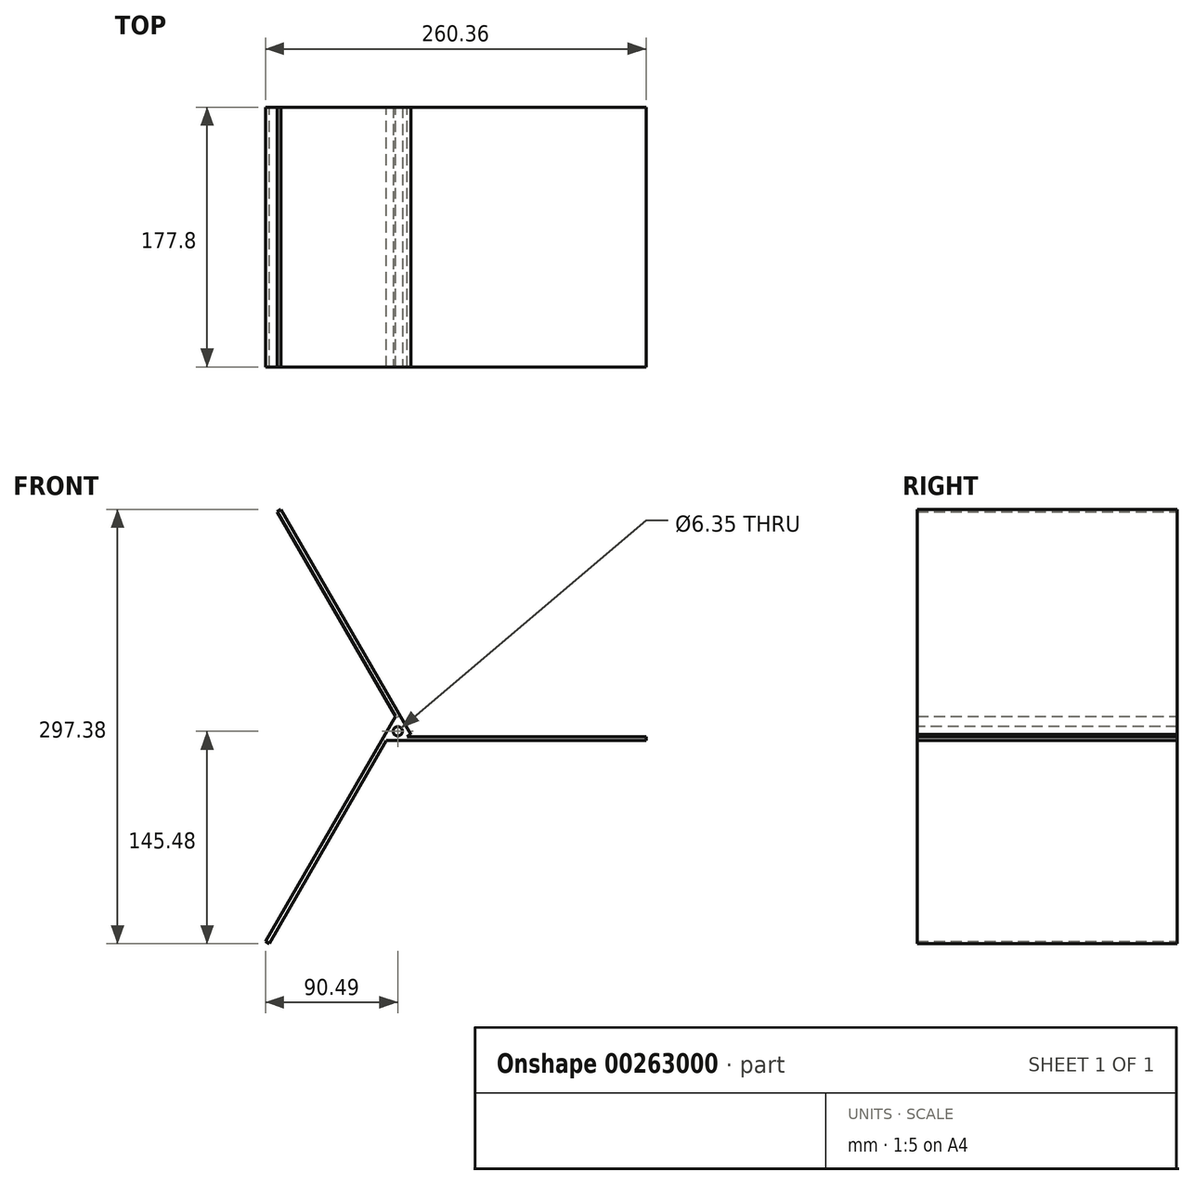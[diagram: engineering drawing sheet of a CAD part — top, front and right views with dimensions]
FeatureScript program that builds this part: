
annotation { "Feature Type Name" : "Feature", "Feature Type Description" : "" }
export const myFeature = defineFeature(function(context is Context, id is Id, definition is map)
    precondition{}
    {
        {
            var Q0;
            Q0=qCreatedBy(makeId("Front.planeOp"),FACE);
            var sketch = newSketch(context, id + "F0", { "sketchPlane" : qUnion([Q0])});
            skCircle(sketch, "E0.cCircle", {"center": v(0, 0) * mm, "radius": 3.67 * mm, "construction": true});
            skLineSegment(sketch, "E0.0", {"start": v(0, 7.33) * mm, "end": v(6.35, -3.67) * mm});
            skLineSegment(sketch, "E0.1", {"start": v(6.35, -3.67) * mm, "end": v(-6.35, -3.67) * mm});
            skLineSegment(sketch, "E0.2", {"start": v(-6.35, -3.67) * mm, "end": v(0, 7.33) * mm});
            skPoint(sketch, "E0.0.midPoint", {"position": v(3.18, 1.83) * mm});
            skLineSegment(sketch, "E1", {"start": v(6.35, -3.67) * mm, "end": v(9.1, -2.08) * mm});
            skLineSegment(sketch, "E2", {"start": v(9.1, -2.08) * mm, "end": v(-79.8, 151.9) * mm});
            skLineSegment(sketch, "E3", {"start": v(-79.8, 151.9) * mm, "end": v(-82.55, 150.31) * mm});
            skLineSegment(sketch, "E4", {"start": v(-82.55, 150.31) * mm, "end": v(0, 7.33) * mm});
            skLineSegment(sketch, "E5", {"start": v(0, 7.33) * mm, "end": v(-1.59, 10.08) * mm});
            skLineSegment(sketch, "E6", {"start": v(-1.59, 10.08) * mm, "end": v(-90.49, -143.9) * mm});
            skLineSegment(sketch, "E7", {"start": v(-90.49, -143.9) * mm, "end": v(-87.74, -145.48) * mm});
            skLineSegment(sketch, "E8", {"start": v(-87.74, -145.48) * mm, "end": v(-6.35, -3.67) * mm});
            skLineSegment(sketch, "E9", {"start": v(-6.35, -3.67) * mm, "end": v(-7.93, -6.42) * mm});
            skLineSegment(sketch, "E10", {"start": v(-7.93, -6.42) * mm, "end": v(169.87, -6.42) * mm});
            skLineSegment(sketch, "E11", {"start": v(6.35, -3.67) * mm, "end": v(169.87, -3.67) * mm});
            skLineSegment(sketch, "E12", {"start": v(169.87, -3.67) * mm, "end": v(169.87, -6.42) * mm});
            skSolve(sketch);
        }
        {
            var Q0;
            Q0=makeQuery(id+"F0.imprint","IMPRINT",FACE,{"disambiguationData":[TD([[makeQuery(id+"F0.imprint","IMPRINT",EDGE,{"derivedFrom":sQuery(id+"F0.wireOp",EDGE,"E0.2")}),1.0]])]});
            var Q1;
            Q1=makeQuery(id+"F0.imprint","IMPRINT",FACE,{"disambiguationData":[TD([[makeQuery(id+"F0.imprint","IMPRINT",EDGE,{"derivedFrom":sQuery(id+"F0.wireOp",EDGE,"E0.0")}),1.0]])]});
            var Q2;
            Q2=makeQuery(id+"F0.imprint","IMPRINT",FACE,{"disambiguationData":[TD([[makeQuery(id+"F0.imprint","IMPRINT",EDGE,{"derivedFrom":sQuery(id+"F0.wireOp",EDGE,"E0.1")}),1.0]])]});
            var Q3;
            Q3=makeQuery(id+"F0.imprint","IMPRINT",FACE,{"disambiguationData":[TD([[makeQuery(id+"F0.imprint","IMPRINT",EDGE,{"derivedFrom":sQuery(id+"F0.wireOp",EDGE,"E0.0")}),-1.0]])]});
            extrude(context, id + "F1", {"entities" : qUnion([Q0, Q1, Q2, Q3]), "depth" : 177.8 * mm});
        }
        {
            var Q0;
            Q0=makeQuery(id+"F1.opExtrude","CAP_FACE",FACE,{"disambiguationData":[OSD([sQuery(id+"F0.wireOp",EDGE,"E1"),sQuery(id+"F0.wireOp",EDGE,"E2"),sQuery(id+"F0.wireOp",EDGE,"E3"),sQuery(id+"F0.wireOp",EDGE,"E4"),sQuery(id+"F0.wireOp",EDGE,"E6"),sQuery(id+"F0.wireOp",EDGE,"E7"),sQuery(id+"F0.wireOp",EDGE,"E8"),sQuery(id+"F0.wireOp",EDGE,"E10"),sQuery(id+"F0.wireOp",EDGE,"E11"),sQuery(id+"F0.wireOp",EDGE,"E12")])],"isStart":false});
            var sketch = newSketch(context, id + "F2", { "sketchPlane" : qUnion([Q0])});
            skCircle(sketch, "E13", {"center": v(0, 0) * mm, "radius": 3.17 * mm});
            skSolve(sketch);
        }
        {
            var Q0;
            Q0=makeQuery(id+"F2.imprint","IMPRINT",FACE,{"disambiguationData":[TD([[makeQuery(id+"F2.imprint","IMPRINT",EDGE,{"derivedFrom":sQuery(id+"F2.wireOp",EDGE,"E13")}),1.0]])]});
            extrude(context, id + "F3", {"entities" : qUnion([Q0]), "operationType" : NewBodyOperationType.REMOVE, "oppositeDirection" : true, "depth" : 177.8 * mm});
        }
    });
